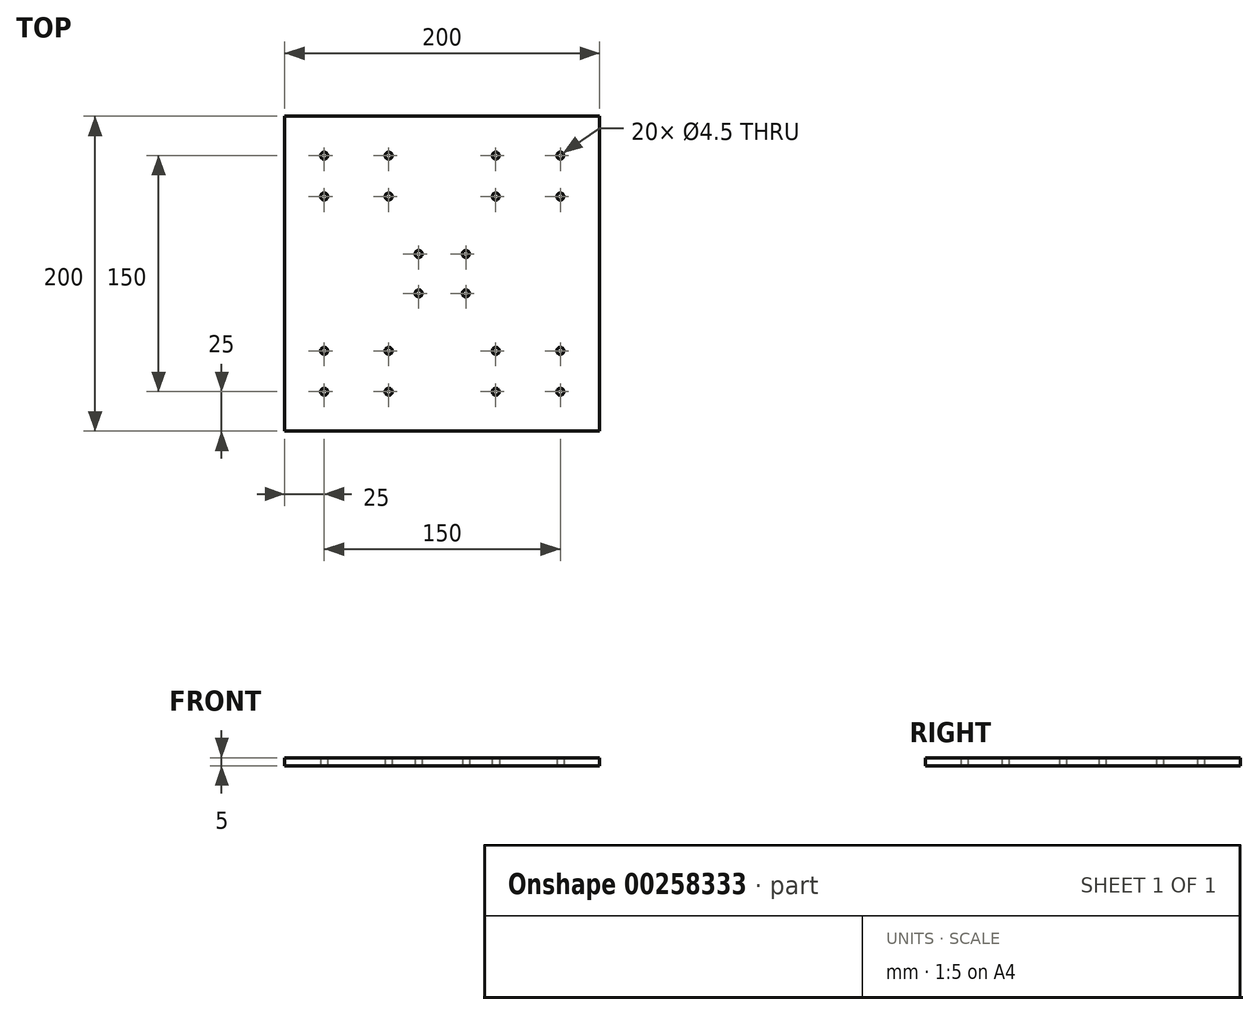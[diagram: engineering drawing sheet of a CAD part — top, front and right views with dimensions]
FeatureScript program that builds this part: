
annotation { "Feature Type Name" : "Feature", "Feature Type Description" : "" }
export const myFeature = defineFeature(function(context is Context, id is Id, definition is map)
    precondition{}
    {
        {
            var Q0;
            Q0=qCreatedBy(makeId("Top.planeOp"),FACE);
            var sketch = newSketch(context, id + "F0", { "sketchPlane" : qUnion([Q0])});
            skLineSegment(sketch, "E0.bottom", {"start": v(100, 100) * mm, "end": v(-100, 100) * mm});
            skLineSegment(sketch, "E0.top", {"start": v(100, -100) * mm, "end": v(-100, -100) * mm});
            skLineSegment(sketch, "E0.left", {"start": v(100, 100) * mm, "end": v(100, -100) * mm});
            skLineSegment(sketch, "E0.right", {"start": v(-100, 100) * mm, "end": v(-100, -100) * mm});
            skPoint(sketch, "E0.middle", {"position": v(0, 0) * mm});
            skCircle(sketch, "E1", {"center": v(-15, 12.5) * mm, "radius": 2.25 * mm});
            skCircle(sketch, "E2", {"center": v(-75, 75) * mm, "radius": 2.25 * mm});
            skCircle(sketch, "E3", {"center": v(-34, 75) * mm, "radius": 2.25 * mm});
            skCircle(sketch, "E4", {"center": v(-75, 49) * mm, "radius": 2.25 * mm});
            skCircle(sketch, "E5", {"center": v(-34, 49) * mm, "radius": 2.25 * mm});
            skCircle(sketch, "E6.MirrorC", {"center": v(34, 49) * mm, "radius": 2.25 * mm});
            skCircle(sketch, "E7.MirrorC", {"center": v(15, 12.5) * mm, "radius": 2.25 * mm});
            skCircle(sketch, "E8.MirrorC", {"center": v(75, 75) * mm, "radius": 2.25 * mm});
            skCircle(sketch, "E9.MirrorC", {"center": v(34, 75) * mm, "radius": 2.25 * mm});
            skCircle(sketch, "E10.MirrorC", {"center": v(75, 49) * mm, "radius": 2.25 * mm});
            skCircle(sketch, "E11.MirrorC", {"center": v(75, -49) * mm, "radius": 2.25 * mm});
            skCircle(sketch, "E12.MirrorC", {"center": v(34, -75) * mm, "radius": 2.25 * mm});
            skCircle(sketch, "E13.MirrorC", {"center": v(75, -75) * mm, "radius": 2.25 * mm});
            skCircle(sketch, "E14.MirrorC", {"center": v(15, -12.5) * mm, "radius": 2.25 * mm});
            skCircle(sketch, "E15.MirrorC", {"center": v(34, -49) * mm, "radius": 2.25 * mm});
            skCircle(sketch, "E16.MirrorC", {"center": v(-15, -12.5) * mm, "radius": 2.25 * mm});
            skCircle(sketch, "E17.MirrorC", {"center": v(-34, -49) * mm, "radius": 2.25 * mm});
            skCircle(sketch, "E18.MirrorC", {"center": v(-75, -49) * mm, "radius": 2.25 * mm});
            skCircle(sketch, "E19.MirrorC", {"center": v(-34, -75) * mm, "radius": 2.25 * mm});
            skCircle(sketch, "E20.MirrorC", {"center": v(-75, -75) * mm, "radius": 2.25 * mm});
            skSolve(sketch);
        }
        {
            var Q0;
            Q0=qSketchRegion(id+"F0",true);
            extrude(context, id + "F1", {"entities" : qUnion([Q0]), "depth" : 5 * mm});
        }
    });
